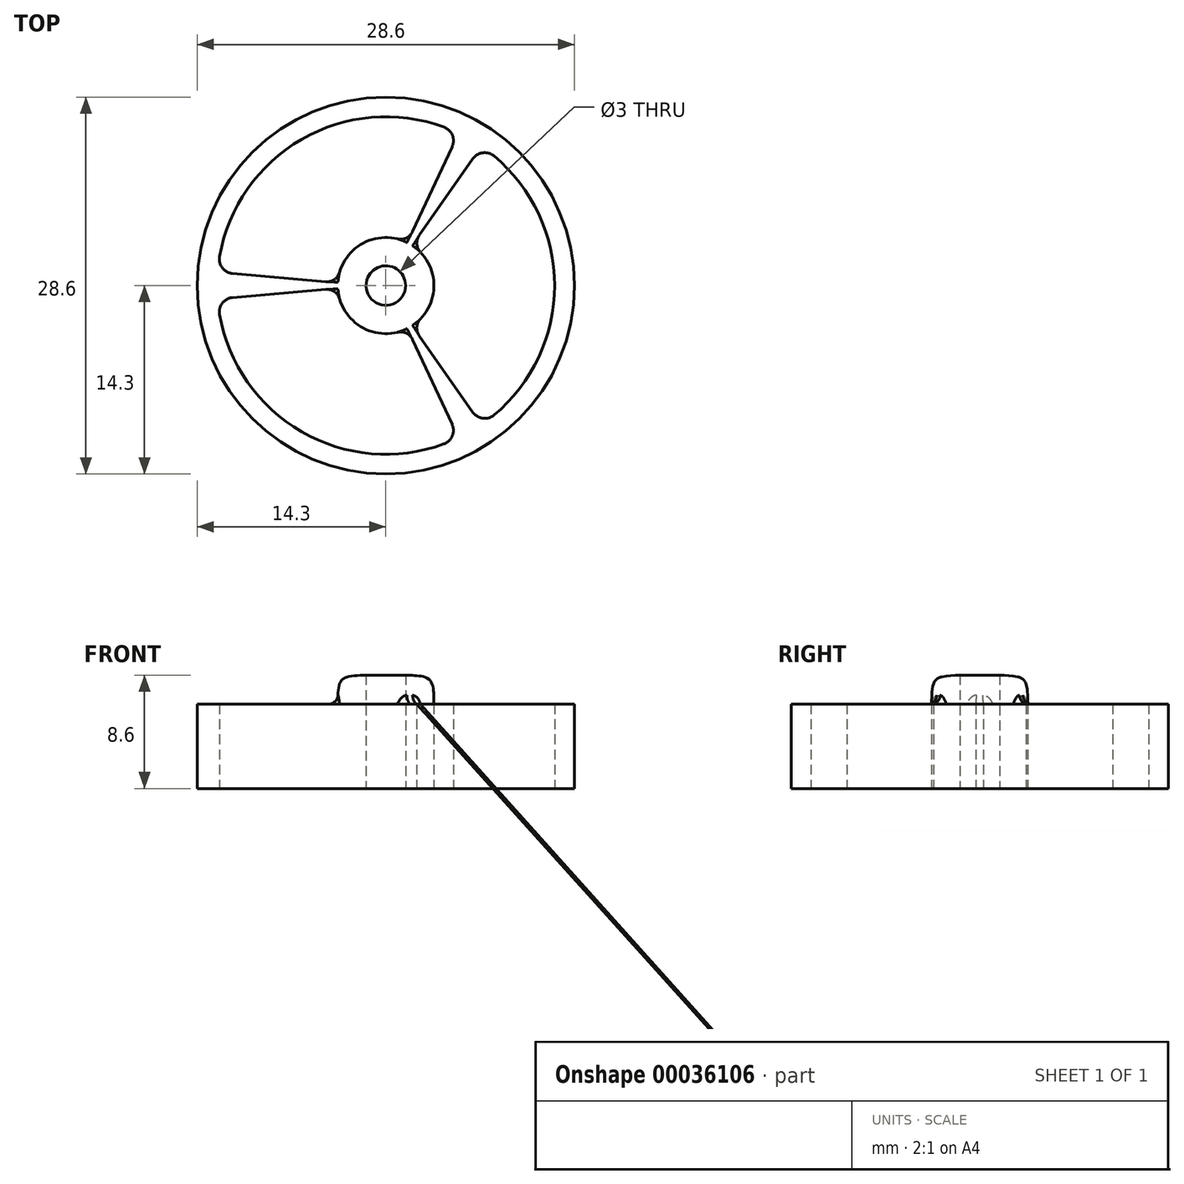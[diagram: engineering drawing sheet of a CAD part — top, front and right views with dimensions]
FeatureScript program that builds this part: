
annotation { "Feature Type Name" : "Feature", "Feature Type Description" : "" }
export const myFeature = defineFeature(function(context is Context, id is Id, definition is map)
    precondition{}
    {
        {
            var Q0;
            Q0=qCreatedBy(makeId("Top.planeOp"),FACE);
            var sketch = newSketch(context, id + "F0", { "sketchPlane" : qUnion([Q0])});
            skCircle(sketch, "E0", {"center": v(0, 0) * mm, "radius": 14.3 * mm});
            skArc(sketch, "E1", {"start": v(-3.5, -1) * mm, "mid": v(-1.82, -3.16) * mm, "end": v(0.88, -3.54) * mm});
            skCircle(sketch, "E2", {"center": v(0, 0) * mm, "radius": 1.5 * mm});
            skArc(sketch, "E3", {"start": v(-12.61, -2.2) * mm, "mid": v(-6.4, -11.09) * mm, "end": v(4.4, -12.02) * mm});
            skLineSegment(sketch, "E4.1.0", {"start": v(2.53, 3.8) * mm, "end": v(6.6, 9.61) * mm});
            skLineSegment(sketch, "E4.1.1", {"start": v(2.03, 4.1) * mm, "end": v(5.03, 10.52) * mm});
            skPoint(sketch, "E5.start.orphan", {"position": v(-3.65, 0) * mm});
            skPoint(sketch, "E6.orphan", {"position": v(-0.09, 0.06) * mm});
            skPoint(sketch, "E7.orphan", {"position": v(0.1, -0.05) * mm});
            skArc(sketch, "E8.trimOffspring", {"start": v(0.88, 3.54) * mm, "mid": v(-1.83, 3.16) * mm, "end": v(-3.5, 1) * mm});
            skLineSegment(sketch, "E9.trimOffspring", {"start": v(-4.56, 0.29) * mm, "end": v(-11.62, 0.9) * mm});
            skLineSegment(sketch, "E10.trimOffspring", {"start": v(-4.56, -0.29) * mm, "end": v(-11.62, -0.9) * mm});
            skLineSegment(sketch, "E11.trimOffspring", {"start": v(-3.64, 0.2) * mm, "end": v(-12.76, 1) * mm, "construction": true});
            skLineSegment(sketch, "E12.trimOffspring", {"start": v(2.53, -3.8) * mm, "end": v(6.6, -9.61) * mm});
            skLineSegment(sketch, "E13.trimOffspring", {"start": v(2.03, -4.1) * mm, "end": v(5.03, -10.52) * mm});
            skLineSegment(sketch, "E14.trimOffspring", {"start": v(1.64, -3.26) * mm, "end": v(5.5, -11.55) * mm, "construction": true});
            skArc(sketch, "E15.trimOffspring", {"start": v(2.63, -2.53) * mm, "mid": v(3.65, 0) * mm, "end": v(2.63, 2.53) * mm});
            skArc(sketch, "E16.trimOffspring", {"start": v(8.2, -9.83) * mm, "mid": v(12.8, 0) * mm, "end": v(8.2, 9.83) * mm});
            skArc(sketch, "E17.trimOffspring", {"start": v(4.4, 12.02) * mm, "mid": v(-6.4, 11.09) * mm, "end": v(-12.61, 2.2) * mm});
            skPoint(sketch, "E18.visualSharp", {"position": v(5.5, 11.55) * mm});
            skArc(sketch, "E18.filletArc", {"start": v(5.03, 10.52) * mm, "mid": v(5.04, 11.4) * mm, "end": v(4.4, 12.02) * mm});
            skPoint(sketch, "E19.visualSharp", {"position": v(7.25, 10.55) * mm});
            skArc(sketch, "E19.filletArc", {"start": v(8.2, 9.83) * mm, "mid": v(7.35, 10.07) * mm, "end": v(6.6, 9.61) * mm});
            skPoint(sketch, "E20.visualSharp", {"position": v(7.25, -10.55) * mm});
            skArc(sketch, "E20.filletArc", {"start": v(6.6, -9.61) * mm, "mid": v(7.35, -10.07) * mm, "end": v(8.2, -9.83) * mm});
            skPoint(sketch, "E21.visualSharp", {"position": v(5.5, -11.55) * mm});
            skArc(sketch, "E21.filletArc", {"start": v(4.4, -12.02) * mm, "mid": v(5.04, -11.4) * mm, "end": v(5.03, -10.52) * mm});
            skPoint(sketch, "E22.visualSharp", {"position": v(-12.76, -1) * mm});
            skArc(sketch, "E22.filletArc", {"start": v(-11.62, -0.9) * mm, "mid": v(-12.4, -1.33) * mm, "end": v(-12.61, -2.2) * mm});
            skPoint(sketch, "E23.visualSharp", {"position": v(-12.76, 1) * mm});
            skArc(sketch, "E23.filletArc", {"start": v(-12.61, 2.2) * mm, "mid": v(-12.4, 1.33) * mm, "end": v(-11.62, 0.9) * mm});
            skPoint(sketch, "E24.visualSharp", {"position": v(-3.64, 0.2) * mm});
            skArc(sketch, "E24.filletArc", {"start": v(-4.56, 0.29) * mm, "mid": v(-3.9, 0.46) * mm, "end": v(-3.5, 1) * mm});
            skPoint(sketch, "E25.visualSharp", {"position": v(-3.64, -0.2) * mm});
            skArc(sketch, "E25.filletArc", {"start": v(-3.5, -1) * mm, "mid": v(-3.9, -0.46) * mm, "end": v(-4.56, -0.29) * mm});
            skPoint(sketch, "E26.visualSharp", {"position": v(1.64, -3.26) * mm});
            skArc(sketch, "E26.filletArc", {"start": v(2.03, -4.1) * mm, "mid": v(1.55, -3.61) * mm, "end": v(0.88, -3.54) * mm});
            skPoint(sketch, "E27.visualSharp", {"position": v(2, -3.05) * mm});
            skArc(sketch, "E27.filletArc", {"start": v(2.63, -2.53) * mm, "mid": v(2.35, -3.15) * mm, "end": v(2.53, -3.8) * mm});
            skPoint(sketch, "E28.visualSharp", {"position": v(2, 3.05) * mm});
            skArc(sketch, "E28.filletArc", {"start": v(2.53, 3.8) * mm, "mid": v(2.35, 3.15) * mm, "end": v(2.63, 2.53) * mm});
            skPoint(sketch, "E29.visualSharp", {"position": v(1.64, 3.26) * mm});
            skArc(sketch, "E29.filletArc", {"start": v(0.88, 3.54) * mm, "mid": v(1.55, 3.61) * mm, "end": v(2.03, 4.1) * mm});
            skSolve(sketch);
        }
        {
            var Q0;
            Q0=makeQuery(id+"F0.imprint","IMPRINT",FACE,{"disambiguationData":[TD([[makeQuery(id+"F0.imprint","IMPRINT",EDGE,{"derivedFrom":sQuery(id+"F0.wireOp",EDGE,"E1")}),1.0]])]});
            extrude(context, id + "F1", {"entities" : qUnion([Q0]), "depth" : 6.4 * mm});
        }
        {
            var Q0;
            Q0=makeQuery(id+"F1.opExtrude","CAP_FACE",FACE,{"disambiguationData":[OSD([sQuery(id+"F0.wireOp",EDGE,"E0"),sQuery(id+"F0.wireOp",EDGE,"E1"),sQuery(id+"F0.wireOp",EDGE,"E2"),sQuery(id+"F0.wireOp",EDGE,"E3"),sQuery(id+"F0.wireOp",EDGE,"E4.1.0"),sQuery(id+"F0.wireOp",EDGE,"E4.1.1"),sQuery(id+"F0.wireOp",EDGE,"E8.trimOffspring"),sQuery(id+"F0.wireOp",EDGE,"E9.trimOffspring"),sQuery(id+"F0.wireOp",EDGE,"E10.trimOffspring"),sQuery(id+"F0.wireOp",EDGE,"E12.trimOffspring"),sQuery(id+"F0.wireOp",EDGE,"E13.trimOffspring"),sQuery(id+"F0.wireOp",EDGE,"E15.trimOffspring"),sQuery(id+"F0.wireOp",EDGE,"E16.trimOffspring"),sQuery(id+"F0.wireOp",EDGE,"E17.trimOffspring"),sQuery(id+"F0.wireOp",EDGE,"E18.filletArc"),sQuery(id+"F0.wireOp",EDGE,"E19.filletArc"),sQuery(id+"F0.wireOp",EDGE,"E20.filletArc"),sQuery(id+"F0.wireOp",EDGE,"E21.filletArc"),sQuery(id+"F0.wireOp",EDGE,"E22.filletArc"),sQuery(id+"F0.wireOp",EDGE,"E23.filletArc"),sQuery(id+"F0.wireOp",EDGE,"E24.filletArc"),sQuery(id+"F0.wireOp",EDGE,"E25.filletArc"),sQuery(id+"F0.wireOp",EDGE,"E26.filletArc"),sQuery(id+"F0.wireOp",EDGE,"E27.filletArc"),sQuery(id+"F0.wireOp",EDGE,"E28.filletArc"),sQuery(id+"F0.wireOp",EDGE,"E29.filletArc")])],"isStart":false});
            var sketch = newSketch(context, id + "F2", { "sketchPlane" : qUnion([Q0])});
            skCircle(sketch, "E30", {"center": v(0, 0) * mm, "radius": 3.65 * mm});
            skPoint(sketch, "E30.first.point", {"position": v(-1.83, 3.16) * mm});
            skPoint(sketch, "E30.second.point", {"position": v(3.65, 0) * mm});
            skPoint(sketch, "E30.third.point", {"position": v(-1.82, -3.16) * mm});
            skSolve(sketch);
        }
        {
            var Q0;
            Q0=makeQuery(id+"F2.imprint","IMPRINT",FACE,{"disambiguationData":[TD([[makeQuery(id+"F2.imprint","IMPRINT",EDGE,{"derivedFrom":makeQuery(id+"F1.opExtrude","CAP_EDGE",EDGE,{"disambiguationData":[OSD([sQuery(id+"F0.wireOp",EDGE,"E2")])],"isStart":false})}),-1.0]])]});
            extrude(context, id + "F3", {"entities" : qUnion([Q0]), "operationType" : NewBodyOperationType.ADD, "depth" : 2.2 * mm});
        }
        {
            var Q0;
            Q0=makeQuery(id+"F3.opExtrude","CAP_EDGE",EDGE,{"disambiguationData":[OSD([sQuery(id+"F2.wireOp",EDGE,"E30")])],"isStart":false});
            fillet(context, id + "F4", {"entities" : qUnion([Q0]), "radius" : 2.2 * mm, "tangentPropagation" : true, "rho" : 0.7, "crossSection" : FilletCrossSection.CONIC, "allowEdgeOverflow" : false});
        }
        {
            var Q0;
            {var subQ0=sQuery(id+"F2.wireOp",EDGE,"E30");Q0=makeQuery(id+"F4.opFillet","BLEND_EDGE",EDGE,{"disambiguationData":[OD(2.0)],"blendedFrom":[makeQuery(id+"F3.opExtrude","CAP_EDGE",EDGE,{"disambiguationData":[OSD([subQ0])],"isStart":false}),makeQuery(id+"F3.boolean.opBoolean","MERGE",FACE,{"derivedFrom":[makeQuery(id+"F1.opExtrude","SWEPT_FACE",FACE,{"disambiguationData":[OSD([sQuery(id+"F0.wireOp",EDGE,"E1")])]}),makeQuery(id+"F1.opExtrude","SWEPT_FACE",FACE,{"disambiguationData":[OSD([sQuery(id+"F0.wireOp",EDGE,"E8.trimOffspring")])]}),makeQuery(id+"F1.opExtrude","SWEPT_FACE",FACE,{"disambiguationData":[OSD([sQuery(id+"F0.wireOp",EDGE,"E15.trimOffspring")])]}),makeQuery(id+"F3.opExtrude","SWEPT_FACE",FACE,{"disambiguationData":[OSD([subQ0])]})]})],"blendedInto":[makeQuery(id+"F3.boolean.opBoolean","MERGE",FACE,{"derivedFrom":[makeQuery(id+"F1.opExtrude","SWEPT_FACE",FACE,{"disambiguationData":[OSD([sQuery(id+"F0.wireOp",EDGE,"E1")])]}),makeQuery(id+"F1.opExtrude","SWEPT_FACE",FACE,{"disambiguationData":[OSD([sQuery(id+"F0.wireOp",EDGE,"E8.trimOffspring")])]}),makeQuery(id+"F1.opExtrude","SWEPT_FACE",FACE,{"disambiguationData":[OSD([sQuery(id+"F0.wireOp",EDGE,"E15.trimOffspring")])]}),makeQuery(id+"F3.opExtrude","SWEPT_FACE",FACE,{"disambiguationData":[OSD([subQ0])]})]})]});}
            var Q1;
            Q1=makeQuery(id+"F4.opFillet","BLEND_EDGE",EDGE,{"disambiguationData":[OD(2.0)],"blendedFrom":[makeQuery(id+"F3.opExtrude","CAP_EDGE",EDGE,{"disambiguationData":[OSD([sQuery(id+"F2.wireOp",EDGE,"E30")])],"isStart":false}),makeQuery(id+"F1.opExtrude","CAP_FACE",FACE,{"disambiguationData":[OSD([sQuery(id+"F0.wireOp",EDGE,"E0"),sQuery(id+"F0.wireOp",EDGE,"E1"),sQuery(id+"F0.wireOp",EDGE,"E2"),sQuery(id+"F0.wireOp",EDGE,"E3"),sQuery(id+"F0.wireOp",EDGE,"E4.1.0"),sQuery(id+"F0.wireOp",EDGE,"E4.1.1"),sQuery(id+"F0.wireOp",EDGE,"E8.trimOffspring"),sQuery(id+"F0.wireOp",EDGE,"E9.trimOffspring"),sQuery(id+"F0.wireOp",EDGE,"E10.trimOffspring"),sQuery(id+"F0.wireOp",EDGE,"E12.trimOffspring"),sQuery(id+"F0.wireOp",EDGE,"E13.trimOffspring"),sQuery(id+"F0.wireOp",EDGE,"E15.trimOffspring"),sQuery(id+"F0.wireOp",EDGE,"E16.trimOffspring"),sQuery(id+"F0.wireOp",EDGE,"E17.trimOffspring"),sQuery(id+"F0.wireOp",EDGE,"E18.filletArc"),sQuery(id+"F0.wireOp",EDGE,"E19.filletArc"),sQuery(id+"F0.wireOp",EDGE,"E20.filletArc"),sQuery(id+"F0.wireOp",EDGE,"E21.filletArc"),sQuery(id+"F0.wireOp",EDGE,"E22.filletArc"),sQuery(id+"F0.wireOp",EDGE,"E23.filletArc"),sQuery(id+"F0.wireOp",EDGE,"E24.filletArc"),sQuery(id+"F0.wireOp",EDGE,"E25.filletArc"),sQuery(id+"F0.wireOp",EDGE,"E26.filletArc"),sQuery(id+"F0.wireOp",EDGE,"E27.filletArc"),sQuery(id+"F0.wireOp",EDGE,"E28.filletArc"),sQuery(id+"F0.wireOp",EDGE,"E29.filletArc")])],"isStart":false})],"blendedInto":[makeQuery(id+"F1.opExtrude","CAP_FACE",FACE,{"disambiguationData":[OSD([sQuery(id+"F0.wireOp",EDGE,"E0"),sQuery(id+"F0.wireOp",EDGE,"E1"),sQuery(id+"F0.wireOp",EDGE,"E2"),sQuery(id+"F0.wireOp",EDGE,"E3"),sQuery(id+"F0.wireOp",EDGE,"E4.1.0"),sQuery(id+"F0.wireOp",EDGE,"E4.1.1"),sQuery(id+"F0.wireOp",EDGE,"E8.trimOffspring"),sQuery(id+"F0.wireOp",EDGE,"E9.trimOffspring"),sQuery(id+"F0.wireOp",EDGE,"E10.trimOffspring"),sQuery(id+"F0.wireOp",EDGE,"E12.trimOffspring"),sQuery(id+"F0.wireOp",EDGE,"E13.trimOffspring"),sQuery(id+"F0.wireOp",EDGE,"E15.trimOffspring"),sQuery(id+"F0.wireOp",EDGE,"E16.trimOffspring"),sQuery(id+"F0.wireOp",EDGE,"E17.trimOffspring"),sQuery(id+"F0.wireOp",EDGE,"E18.filletArc"),sQuery(id+"F0.wireOp",EDGE,"E19.filletArc"),sQuery(id+"F0.wireOp",EDGE,"E20.filletArc"),sQuery(id+"F0.wireOp",EDGE,"E21.filletArc"),sQuery(id+"F0.wireOp",EDGE,"E22.filletArc"),sQuery(id+"F0.wireOp",EDGE,"E23.filletArc"),sQuery(id+"F0.wireOp",EDGE,"E24.filletArc"),sQuery(id+"F0.wireOp",EDGE,"E25.filletArc"),sQuery(id+"F0.wireOp",EDGE,"E26.filletArc"),sQuery(id+"F0.wireOp",EDGE,"E27.filletArc"),sQuery(id+"F0.wireOp",EDGE,"E28.filletArc"),sQuery(id+"F0.wireOp",EDGE,"E29.filletArc")])],"isStart":false})]});
            var Q2;
            {var subQ0=sQuery(id+"F2.wireOp",EDGE,"E30");Q2=makeQuery(id+"F4.opFillet","BLEND_EDGE",EDGE,{"disambiguationData":[OD(0.0)],"blendedFrom":[makeQuery(id+"F3.opExtrude","CAP_EDGE",EDGE,{"disambiguationData":[OSD([subQ0])],"isStart":false}),makeQuery(id+"F3.boolean.opBoolean","MERGE",FACE,{"derivedFrom":[makeQuery(id+"F1.opExtrude","SWEPT_FACE",FACE,{"disambiguationData":[OSD([sQuery(id+"F0.wireOp",EDGE,"E1")])]}),makeQuery(id+"F1.opExtrude","SWEPT_FACE",FACE,{"disambiguationData":[OSD([sQuery(id+"F0.wireOp",EDGE,"E8.trimOffspring")])]}),makeQuery(id+"F1.opExtrude","SWEPT_FACE",FACE,{"disambiguationData":[OSD([sQuery(id+"F0.wireOp",EDGE,"E15.trimOffspring")])]}),makeQuery(id+"F3.opExtrude","SWEPT_FACE",FACE,{"disambiguationData":[OSD([subQ0])]})]})],"blendedInto":[makeQuery(id+"F3.boolean.opBoolean","MERGE",FACE,{"derivedFrom":[makeQuery(id+"F1.opExtrude","SWEPT_FACE",FACE,{"disambiguationData":[OSD([sQuery(id+"F0.wireOp",EDGE,"E1")])]}),makeQuery(id+"F1.opExtrude","SWEPT_FACE",FACE,{"disambiguationData":[OSD([sQuery(id+"F0.wireOp",EDGE,"E8.trimOffspring")])]}),makeQuery(id+"F1.opExtrude","SWEPT_FACE",FACE,{"disambiguationData":[OSD([sQuery(id+"F0.wireOp",EDGE,"E15.trimOffspring")])]}),makeQuery(id+"F3.opExtrude","SWEPT_FACE",FACE,{"disambiguationData":[OSD([subQ0])]})]})]});}
            var Q3;
            Q3=makeQuery(id+"F4.opFillet","BLEND_EDGE",EDGE,{"disambiguationData":[OD(1.0)],"blendedFrom":[makeQuery(id+"F3.opExtrude","CAP_EDGE",EDGE,{"disambiguationData":[OSD([sQuery(id+"F2.wireOp",EDGE,"E30")])],"isStart":false}),makeQuery(id+"F1.opExtrude","CAP_FACE",FACE,{"disambiguationData":[OSD([sQuery(id+"F0.wireOp",EDGE,"E0"),sQuery(id+"F0.wireOp",EDGE,"E1"),sQuery(id+"F0.wireOp",EDGE,"E2"),sQuery(id+"F0.wireOp",EDGE,"E3"),sQuery(id+"F0.wireOp",EDGE,"E4.1.0"),sQuery(id+"F0.wireOp",EDGE,"E4.1.1"),sQuery(id+"F0.wireOp",EDGE,"E8.trimOffspring"),sQuery(id+"F0.wireOp",EDGE,"E9.trimOffspring"),sQuery(id+"F0.wireOp",EDGE,"E10.trimOffspring"),sQuery(id+"F0.wireOp",EDGE,"E12.trimOffspring"),sQuery(id+"F0.wireOp",EDGE,"E13.trimOffspring"),sQuery(id+"F0.wireOp",EDGE,"E15.trimOffspring"),sQuery(id+"F0.wireOp",EDGE,"E16.trimOffspring"),sQuery(id+"F0.wireOp",EDGE,"E17.trimOffspring"),sQuery(id+"F0.wireOp",EDGE,"E18.filletArc"),sQuery(id+"F0.wireOp",EDGE,"E19.filletArc"),sQuery(id+"F0.wireOp",EDGE,"E20.filletArc"),sQuery(id+"F0.wireOp",EDGE,"E21.filletArc"),sQuery(id+"F0.wireOp",EDGE,"E22.filletArc"),sQuery(id+"F0.wireOp",EDGE,"E23.filletArc"),sQuery(id+"F0.wireOp",EDGE,"E24.filletArc"),sQuery(id+"F0.wireOp",EDGE,"E25.filletArc"),sQuery(id+"F0.wireOp",EDGE,"E26.filletArc"),sQuery(id+"F0.wireOp",EDGE,"E27.filletArc"),sQuery(id+"F0.wireOp",EDGE,"E28.filletArc"),sQuery(id+"F0.wireOp",EDGE,"E29.filletArc")])],"isStart":false})],"blendedInto":[makeQuery(id+"F1.opExtrude","CAP_FACE",FACE,{"disambiguationData":[OSD([sQuery(id+"F0.wireOp",EDGE,"E0"),sQuery(id+"F0.wireOp",EDGE,"E1"),sQuery(id+"F0.wireOp",EDGE,"E2"),sQuery(id+"F0.wireOp",EDGE,"E3"),sQuery(id+"F0.wireOp",EDGE,"E4.1.0"),sQuery(id+"F0.wireOp",EDGE,"E4.1.1"),sQuery(id+"F0.wireOp",EDGE,"E8.trimOffspring"),sQuery(id+"F0.wireOp",EDGE,"E9.trimOffspring"),sQuery(id+"F0.wireOp",EDGE,"E10.trimOffspring"),sQuery(id+"F0.wireOp",EDGE,"E12.trimOffspring"),sQuery(id+"F0.wireOp",EDGE,"E13.trimOffspring"),sQuery(id+"F0.wireOp",EDGE,"E15.trimOffspring"),sQuery(id+"F0.wireOp",EDGE,"E16.trimOffspring"),sQuery(id+"F0.wireOp",EDGE,"E17.trimOffspring"),sQuery(id+"F0.wireOp",EDGE,"E18.filletArc"),sQuery(id+"F0.wireOp",EDGE,"E19.filletArc"),sQuery(id+"F0.wireOp",EDGE,"E20.filletArc"),sQuery(id+"F0.wireOp",EDGE,"E21.filletArc"),sQuery(id+"F0.wireOp",EDGE,"E22.filletArc"),sQuery(id+"F0.wireOp",EDGE,"E23.filletArc"),sQuery(id+"F0.wireOp",EDGE,"E24.filletArc"),sQuery(id+"F0.wireOp",EDGE,"E25.filletArc"),sQuery(id+"F0.wireOp",EDGE,"E26.filletArc"),sQuery(id+"F0.wireOp",EDGE,"E27.filletArc"),sQuery(id+"F0.wireOp",EDGE,"E28.filletArc"),sQuery(id+"F0.wireOp",EDGE,"E29.filletArc")])],"isStart":false})]});
            var Q4;
            {var subQ0=sQuery(id+"F2.wireOp",EDGE,"E30");Q4=makeQuery(id+"F4.opFillet","BLEND_EDGE",EDGE,{"disambiguationData":[OD(1.0)],"blendedFrom":[makeQuery(id+"F3.opExtrude","CAP_EDGE",EDGE,{"disambiguationData":[OSD([subQ0])],"isStart":false}),makeQuery(id+"F3.boolean.opBoolean","MERGE",FACE,{"derivedFrom":[makeQuery(id+"F1.opExtrude","SWEPT_FACE",FACE,{"disambiguationData":[OSD([sQuery(id+"F0.wireOp",EDGE,"E1")])]}),makeQuery(id+"F1.opExtrude","SWEPT_FACE",FACE,{"disambiguationData":[OSD([sQuery(id+"F0.wireOp",EDGE,"E8.trimOffspring")])]}),makeQuery(id+"F1.opExtrude","SWEPT_FACE",FACE,{"disambiguationData":[OSD([sQuery(id+"F0.wireOp",EDGE,"E15.trimOffspring")])]}),makeQuery(id+"F3.opExtrude","SWEPT_FACE",FACE,{"disambiguationData":[OSD([subQ0])]})]})],"blendedInto":[makeQuery(id+"F3.boolean.opBoolean","MERGE",FACE,{"derivedFrom":[makeQuery(id+"F1.opExtrude","SWEPT_FACE",FACE,{"disambiguationData":[OSD([sQuery(id+"F0.wireOp",EDGE,"E1")])]}),makeQuery(id+"F1.opExtrude","SWEPT_FACE",FACE,{"disambiguationData":[OSD([sQuery(id+"F0.wireOp",EDGE,"E8.trimOffspring")])]}),makeQuery(id+"F1.opExtrude","SWEPT_FACE",FACE,{"disambiguationData":[OSD([sQuery(id+"F0.wireOp",EDGE,"E15.trimOffspring")])]}),makeQuery(id+"F3.opExtrude","SWEPT_FACE",FACE,{"disambiguationData":[OSD([subQ0])]})]})]});}
            var Q5;
            Q5=makeQuery(id+"F4.opFillet","BLEND_EDGE",EDGE,{"disambiguationData":[OD(0.0)],"blendedFrom":[makeQuery(id+"F3.opExtrude","CAP_EDGE",EDGE,{"disambiguationData":[OSD([sQuery(id+"F2.wireOp",EDGE,"E30")])],"isStart":false}),makeQuery(id+"F1.opExtrude","CAP_FACE",FACE,{"disambiguationData":[OSD([sQuery(id+"F0.wireOp",EDGE,"E0"),sQuery(id+"F0.wireOp",EDGE,"E1"),sQuery(id+"F0.wireOp",EDGE,"E2"),sQuery(id+"F0.wireOp",EDGE,"E3"),sQuery(id+"F0.wireOp",EDGE,"E4.1.0"),sQuery(id+"F0.wireOp",EDGE,"E4.1.1"),sQuery(id+"F0.wireOp",EDGE,"E8.trimOffspring"),sQuery(id+"F0.wireOp",EDGE,"E9.trimOffspring"),sQuery(id+"F0.wireOp",EDGE,"E10.trimOffspring"),sQuery(id+"F0.wireOp",EDGE,"E12.trimOffspring"),sQuery(id+"F0.wireOp",EDGE,"E13.trimOffspring"),sQuery(id+"F0.wireOp",EDGE,"E15.trimOffspring"),sQuery(id+"F0.wireOp",EDGE,"E16.trimOffspring"),sQuery(id+"F0.wireOp",EDGE,"E17.trimOffspring"),sQuery(id+"F0.wireOp",EDGE,"E18.filletArc"),sQuery(id+"F0.wireOp",EDGE,"E19.filletArc"),sQuery(id+"F0.wireOp",EDGE,"E20.filletArc"),sQuery(id+"F0.wireOp",EDGE,"E21.filletArc"),sQuery(id+"F0.wireOp",EDGE,"E22.filletArc"),sQuery(id+"F0.wireOp",EDGE,"E23.filletArc"),sQuery(id+"F0.wireOp",EDGE,"E24.filletArc"),sQuery(id+"F0.wireOp",EDGE,"E25.filletArc"),sQuery(id+"F0.wireOp",EDGE,"E26.filletArc"),sQuery(id+"F0.wireOp",EDGE,"E27.filletArc"),sQuery(id+"F0.wireOp",EDGE,"E28.filletArc"),sQuery(id+"F0.wireOp",EDGE,"E29.filletArc")])],"isStart":false})],"blendedInto":[makeQuery(id+"F1.opExtrude","CAP_FACE",FACE,{"disambiguationData":[OSD([sQuery(id+"F0.wireOp",EDGE,"E0"),sQuery(id+"F0.wireOp",EDGE,"E1"),sQuery(id+"F0.wireOp",EDGE,"E2"),sQuery(id+"F0.wireOp",EDGE,"E3"),sQuery(id+"F0.wireOp",EDGE,"E4.1.0"),sQuery(id+"F0.wireOp",EDGE,"E4.1.1"),sQuery(id+"F0.wireOp",EDGE,"E8.trimOffspring"),sQuery(id+"F0.wireOp",EDGE,"E9.trimOffspring"),sQuery(id+"F0.wireOp",EDGE,"E10.trimOffspring"),sQuery(id+"F0.wireOp",EDGE,"E12.trimOffspring"),sQuery(id+"F0.wireOp",EDGE,"E13.trimOffspring"),sQuery(id+"F0.wireOp",EDGE,"E15.trimOffspring"),sQuery(id+"F0.wireOp",EDGE,"E16.trimOffspring"),sQuery(id+"F0.wireOp",EDGE,"E17.trimOffspring"),sQuery(id+"F0.wireOp",EDGE,"E18.filletArc"),sQuery(id+"F0.wireOp",EDGE,"E19.filletArc"),sQuery(id+"F0.wireOp",EDGE,"E20.filletArc"),sQuery(id+"F0.wireOp",EDGE,"E21.filletArc"),sQuery(id+"F0.wireOp",EDGE,"E22.filletArc"),sQuery(id+"F0.wireOp",EDGE,"E23.filletArc"),sQuery(id+"F0.wireOp",EDGE,"E24.filletArc"),sQuery(id+"F0.wireOp",EDGE,"E25.filletArc"),sQuery(id+"F0.wireOp",EDGE,"E26.filletArc"),sQuery(id+"F0.wireOp",EDGE,"E27.filletArc"),sQuery(id+"F0.wireOp",EDGE,"E28.filletArc"),sQuery(id+"F0.wireOp",EDGE,"E29.filletArc")])],"isStart":false})]});
            fillet(context, id + "F5", {"entities" : qUnion([Q0, Q1, Q2, Q3, Q4, Q5]), "radius" : 0.7 * mm, "tangentPropagation" : true, "allowEdgeOverflow" : false});
        }
    });
